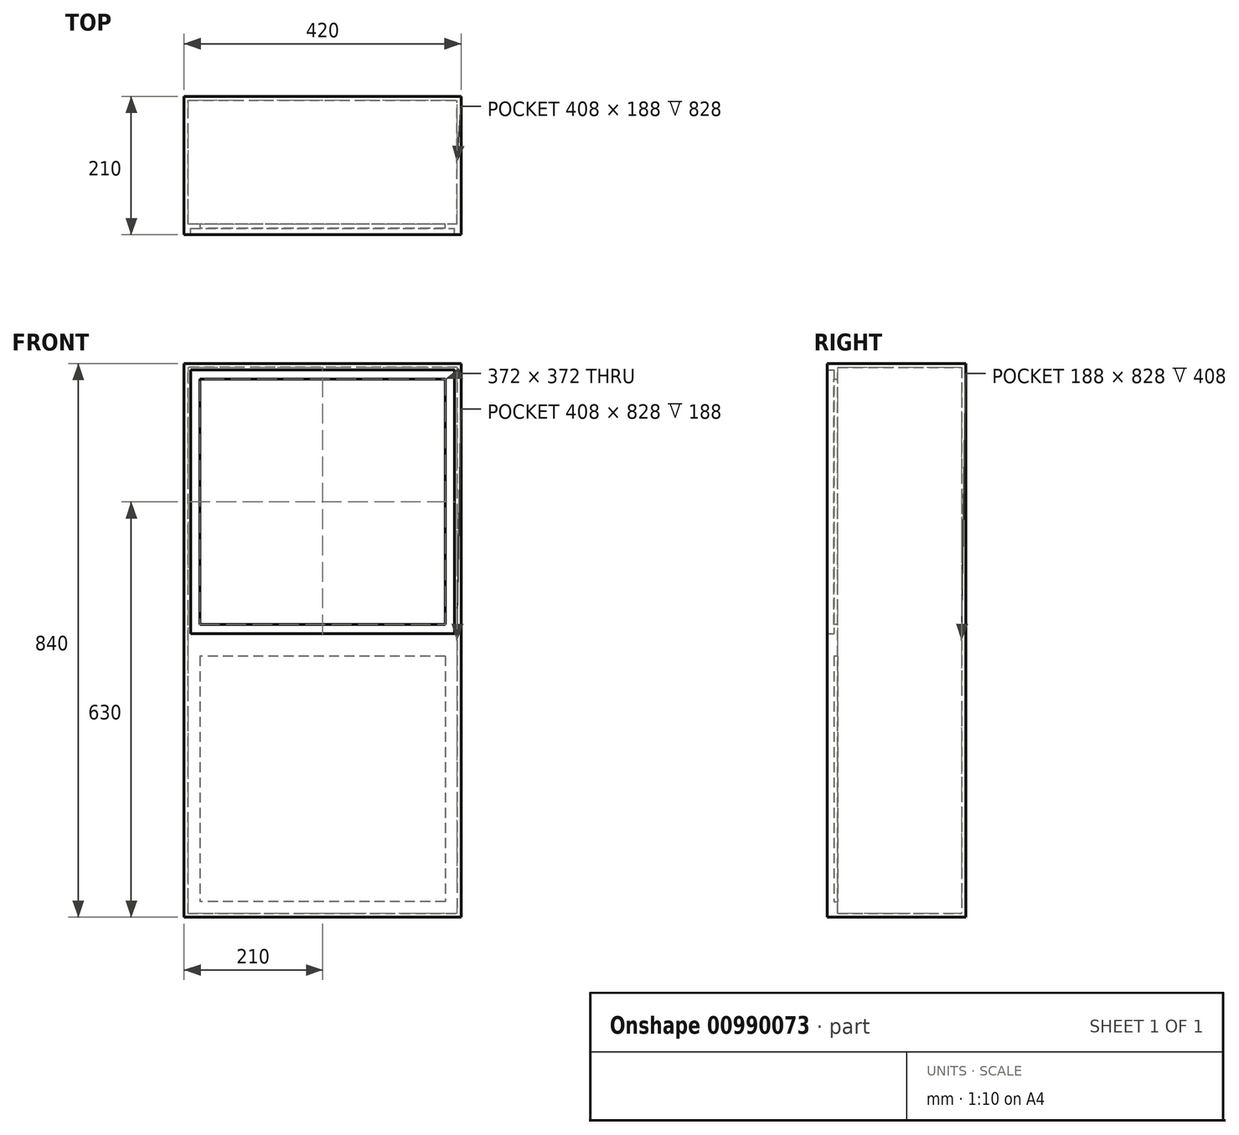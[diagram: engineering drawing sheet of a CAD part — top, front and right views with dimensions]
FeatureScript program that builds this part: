
annotation { "Feature Type Name" : "Feature", "Feature Type Description" : "" }
export const myFeature = defineFeature(function(context is Context, id is Id, definition is map)
    precondition{}
    {
        {
            var Q0;
            Q0=qCreatedBy(makeId("Front.planeOp"),FACE);
            var sketch = newSketch(context, id + "F0", { "sketchPlane" : qUnion([Q0])});
            skLineSegment(sketch, "E0.bottom", {"start": v(-210, 210) * mm, "end": v(210, 210) * mm});
            skLineSegment(sketch, "E0.top", {"start": v(-210, -210) * mm, "end": v(210, -210) * mm});
            skLineSegment(sketch, "E0.left", {"start": v(-210, 210) * mm, "end": v(-210, -210) * mm});
            skLineSegment(sketch, "E0.right", {"start": v(210, 210) * mm, "end": v(210, -210) * mm});
            skPoint(sketch, "E0.middle", {"position": v(0, 0) * mm});
            skSolve(sketch);
        }
        {
            var Q0;
            Q0=qSketchRegion(id+"F0",true);
            extrude(context, id + "F1", {"entities" : qUnion([Q0]), "endBound" : BoundingType.SYMMETRIC, "depth" : 210 * mm, "offsetDistance" : 25.4 * mm});
        }
        {
            var Q0;
            Q0=makeQuery(id+"F1.opExtrude","CAP_FACE",FACE,{"disambiguationData":[OSD([sQuery(id+"F0.wireOp",EDGE,"E0.bottom"),sQuery(id+"F0.wireOp",EDGE,"E0.top"),sQuery(id+"F0.wireOp",EDGE,"E0.left"),sQuery(id+"F0.wireOp",EDGE,"E0.right")])],"isStart":false});
            shell(context, id + "F2", {"entities" : qUnion([Q0]), "thickness" : 6 * mm});
        }
        {
            var Q0;
            Q0=makeQuery(id+"F2.opShell","OFFSET_FACE",FACE,{"disambiguationData":[OSD([sQuery(id+"F0.wireOp",EDGE,"E0.left")])]});
            var sketch = newSketch(context, id + "F3", { "sketchPlane" : qUnion([Q0])});
            skLineSegment(sketch, "E1.top", {"start": v(-2, -194) * mm, "end": v(2, -194) * mm});
            skPoint(sketch, "E1.middle", {"position": v(0, 0) * mm});
            skLineSegment(sketch, "E2.bottom", {"start": v(-89, -204) * mm, "end": v(-95, -204) * mm});
            skLineSegment(sketch, "E2.top", {"start": v(-89, 204) * mm, "end": v(-95, 204) * mm});
            skLineSegment(sketch, "E2.left", {"start": v(-89, -204) * mm, "end": v(-89, 204) * mm});
            skLineSegment(sketch, "E2.right", {"start": v(-95, -204) * mm, "end": v(-95, 204) * mm});
            skPoint(sketch, "E2.middle", {"position": v(-92, 0) * mm});
            skSolve(sketch);
        }
        {
            var Q0;
            Q0=qSketchRegion(id+"F3",true);
            extrude(context, id + "F4", {"entities" : qUnion([Q0]), "operationType" : NewBodyOperationType.ADD, "depth" : 18 * mm, "offsetDistance" : 25.4 * mm});
        }
        {
            var Q0;
            Q0=makeQuery(id+"F2.opShell","OFFSET_FACE",FACE,{"disambiguationData":[OSD([sQuery(id+"F0.wireOp",EDGE,"E0.right")])]});
            var sketch = newSketch(context, id + "F5", { "sketchPlane" : qUnion([Q0])});
            skLineSegment(sketch, "E3.bottom", {"start": v(95, -204) * mm, "end": v(89, -204) * mm});
            skLineSegment(sketch, "E3.top", {"start": v(95, 204) * mm, "end": v(89, 204) * mm});
            skLineSegment(sketch, "E3.left", {"start": v(89, -204) * mm, "end": v(89, 204) * mm});
            skLineSegment(sketch, "E3.right", {"start": v(95, -204) * mm, "end": v(95, 204) * mm});
            skPoint(sketch, "E3.middle", {"position": v(92, 0) * mm});
            skSolve(sketch);
        }
        {
            var Q0;
            Q0=qSketchRegion(id+"F5",true);
            extrude(context, id + "F6", {"entities" : qUnion([Q0]), "operationType" : NewBodyOperationType.ADD, "depth" : 18 * mm, "offsetDistance" : 25.4 * mm});
        }
        {
            var Q0;
            Q0=makeQuery(id+"F4.opExtrude","CAP_FACE",FACE,{"disambiguationData":[OSD([sQuery(id+"F3.wireOp",EDGE,"E2.bottom"),sQuery(id+"F3.wireOp",EDGE,"E2.top"),sQuery(id+"F3.wireOp",EDGE,"E2.left"),sQuery(id+"F3.wireOp",EDGE,"E2.right")])],"isStart":false});
            var sketch = newSketch(context, id + "F7", { "sketchPlane" : qUnion([Q0])});
            skLineSegment(sketch, "E4.bottom", {"start": v(-95, 204) * mm, "end": v(-89, 204) * mm});
            skLineSegment(sketch, "E4.top", {"start": v(-95, 186) * mm, "end": v(-89, 186) * mm});
            skLineSegment(sketch, "E4.left", {"start": v(-95, 204) * mm, "end": v(-95, 186) * mm});
            skLineSegment(sketch, "E4.right", {"start": v(-89, 204) * mm, "end": v(-89, 186) * mm});
            skSolve(sketch);
        }
        {
            var Q0;
            Q0=qSketchRegion(id+"F7",true);
            var Q1;
            Q1=makeQuery(id+"F6.opExtrude","CAP_FACE",FACE,{"disambiguationData":[OSD([sQuery(id+"F5.wireOp",EDGE,"E3.bottom"),sQuery(id+"F5.wireOp",EDGE,"E3.top"),sQuery(id+"F5.wireOp",EDGE,"E3.left"),sQuery(id+"F5.wireOp",EDGE,"E3.right")])],"isStart":false});
            extrude(context, id + "F8", {"entities" : qUnion([Q0]), "operationType" : NewBodyOperationType.ADD, "endBound" : BoundingType.UP_TO_SURFACE, "depth" : 12.2 * mm, "endBoundEntityFace" : qUnion([Q1]), "offsetDistance" : 25.4 * mm});
        }
        {
            var Q0;
            Q0=makeQuery(id+"F4.opExtrude","CAP_FACE",FACE,{"disambiguationData":[OSD([sQuery(id+"F3.wireOp",EDGE,"E2.bottom"),sQuery(id+"F3.wireOp",EDGE,"E2.top"),sQuery(id+"F3.wireOp",EDGE,"E2.left"),sQuery(id+"F3.wireOp",EDGE,"E2.right")])],"isStart":false});
            var sketch = newSketch(context, id + "F9", { "sketchPlane" : qUnion([Q0])});
            skLineSegment(sketch, "E5.bottom", {"start": v(-89, -204) * mm, "end": v(-95, -204) * mm});
            skLineSegment(sketch, "E5.top", {"start": v(-89, -186) * mm, "end": v(-95, -186) * mm});
            skLineSegment(sketch, "E5.left", {"start": v(-89, -204) * mm, "end": v(-89, -186) * mm});
            skLineSegment(sketch, "E5.right", {"start": v(-95, -204) * mm, "end": v(-95, -186) * mm});
            skSolve(sketch);
        }
        {
            var Q0;
            Q0=qSketchRegion(id+"F9",true);
            var Q1;
            Q1=makeQuery(id+"F6.opExtrude","CAP_FACE",FACE,{"disambiguationData":[OSD([sQuery(id+"F5.wireOp",EDGE,"E3.bottom"),sQuery(id+"F5.wireOp",EDGE,"E3.top"),sQuery(id+"F5.wireOp",EDGE,"E3.left"),sQuery(id+"F5.wireOp",EDGE,"E3.right")])],"isStart":false});
            extrude(context, id + "F10", {"entities" : qUnion([Q0]), "operationType" : NewBodyOperationType.ADD, "endBound" : BoundingType.UP_TO_SURFACE, "depth" : 25.4 * mm, "endBoundEntityFace" : qUnion([Q1]), "offsetDistance" : 25.4 * mm});
        }
        {
            var Q0;
            Q0=makeQuery(id+"F10.boolean.opBoolean","MERGE",FACE,{"derivedFrom":[makeQuery(id+"F8.boolean.opBoolean","MERGE",FACE,{"derivedFrom":[makeQuery(id+"F4.opExtrude","SWEPT_FACE",FACE,{"disambiguationData":[OSD([sQuery(id+"F3.wireOp",EDGE,"E2.right")])]}),makeQuery(id+"F6.opExtrude","SWEPT_FACE",FACE,{"disambiguationData":[OSD([sQuery(id+"F5.wireOp",EDGE,"E3.right")])]}),makeQuery(id+"F8.opExtrude","SWEPT_FACE",FACE,{"disambiguationData":[OSD([sQuery(id+"F7.wireOp",EDGE,"E4.left")])]})]}),makeQuery(id+"F10.opExtrude","SWEPT_FACE",FACE,{"disambiguationData":[OSD([sQuery(id+"F9.wireOp",EDGE,"E5.right")])]})]});
            var sketch = newSketch(context, id + "F11", { "sketchPlane" : qUnion([Q0])});
            skLineSegment(sketch, "E6.bottom", {"start": v(-204, 204) * mm, "end": v(204, 204) * mm});
            skLineSegment(sketch, "E6.top", {"start": v(-204, -204) * mm, "end": v(204, -204) * mm});
            skLineSegment(sketch, "E6.left", {"start": v(-204, 204) * mm, "end": v(-204, -204) * mm});
            skLineSegment(sketch, "E6.right", {"start": v(204, 204) * mm, "end": v(204, -204) * mm});
            skPoint(sketch, "E6.middle", {"position": v(0, 0) * mm});
            skLineSegment(sketch, "E7.bottom", {"start": v(-200, 200) * mm, "end": v(200, 200) * mm});
            skLineSegment(sketch, "E7.top", {"start": v(-200, -200) * mm, "end": v(200, -200) * mm});
            skLineSegment(sketch, "E7.left", {"start": v(-200, 200) * mm, "end": v(-200, -200) * mm});
            skLineSegment(sketch, "E7.right", {"start": v(200, 200) * mm, "end": v(200, -200) * mm});
            skSolve(sketch);
        }
        {
            var Q0;
            Q0=qSketchRegion(id+"F11",true);
            extrude(context, id + "F12", {"entities" : qUnion([Q0]), "operationType" : NewBodyOperationType.ADD, "depth" : 10 * mm, "offsetDistance" : 25.4 * mm});
        }
        {
            var Q0;
            Q0=makeQuery(id+"F1.opExtrude","SWEPT_BODY",BODY,{"disambiguationData":[OSD([sQuery(id+"F0.wireOp",EDGE,"E0.bottom"),sQuery(id+"F0.wireOp",EDGE,"E0.top"),sQuery(id+"F0.wireOp",EDGE,"E0.left"),sQuery(id+"F0.wireOp",EDGE,"E0.right")])]});
            var Q1;
            Q1=makeQuery(id+"F1.opExtrude","SWEPT_FACE",FACE,{"disambiguationData":[OSD([sQuery(id+"F0.wireOp",EDGE,"E0.top")])]});
            mirror(context, id + "F13", {"operationType" : NewBodyOperationType.ADD, "entities" : qUnion([Q0]), "mirrorPlane" : qUnion([Q1])});
        }
        {
            var Q0;
            Q0=makeQuery(id+"F13.opPattern","COPY",FACE,{"derivedFrom":makeQuery(id+"F10.boolean.opBoolean","MERGE",FACE,{"derivedFrom":[makeQuery(id+"F8.boolean.opBoolean","MERGE",FACE,{"derivedFrom":[makeQuery(id+"F4.opExtrude","SWEPT_FACE",FACE,{"disambiguationData":[OSD([sQuery(id+"F3.wireOp",EDGE,"E2.right")])]}),makeQuery(id+"F6.opExtrude","SWEPT_FACE",FACE,{"disambiguationData":[OSD([sQuery(id+"F5.wireOp",EDGE,"E3.right")])]}),makeQuery(id+"F8.opExtrude","SWEPT_FACE",FACE,{"disambiguationData":[OSD([sQuery(id+"F7.wireOp",EDGE,"E4.left")])]})]}),makeQuery(id+"F10.opExtrude","SWEPT_FACE",FACE,{"disambiguationData":[OSD([sQuery(id+"F9.wireOp",EDGE,"E5.right")])]})]}),"instanceName":"1"});
            var sketch = newSketch(context, id + "F14", { "sketchPlane" : qUnion([Q0])});
            skLineSegment(sketch, "E8.bottom", {"start": v(-200, -220) * mm, "end": v(200, -220) * mm});
            skLineSegment(sketch, "E8.top", {"start": v(-200, -620) * mm, "end": v(200, -620) * mm});
            skLineSegment(sketch, "E8.left", {"start": v(-200, -220) * mm, "end": v(-200, -620) * mm});
            skLineSegment(sketch, "E8.right", {"start": v(200, -220) * mm, "end": v(200, -620) * mm});
            skSolve(sketch);
        }
        {
            var Q0;
            Q0=qSketchRegion(id+"F14",true);
            extrude(context, id + "F15", {"entities" : qUnion([Q0]), "operationType" : NewBodyOperationType.ADD, "depth" : 10 * mm, "offsetDistance" : 25.4 * mm});
        }
        {
            var Q0;
            {var subQ2=sQuery(id+"F0.wireOp",EDGE,"E0.top");Q0=makeQuery(id+"F10.boolean.opBoolean","SPLIT",FACE,{"disambiguationData":[TD([makeQuery(id+"F4.opExtrude","SWEPT_FACE",FACE,{"disambiguationData":[OSD([sQuery(id+"F3.wireOp",EDGE,"E2.left")])]})])],"derivedFrom":makeQuery(id+"F2.opShell","OFFSET_FACE",FACE,{"disambiguationData":[OSD([subQ2])]})});}
            extrude(context, id + "F16", {"entities" : qUnion([Q0]), "operationType" : NewBodyOperationType.REMOVE, "oppositeDirection" : true, "depth" : 25.4 * mm, "offsetDistance" : 25.4 * mm});
        }
    });
